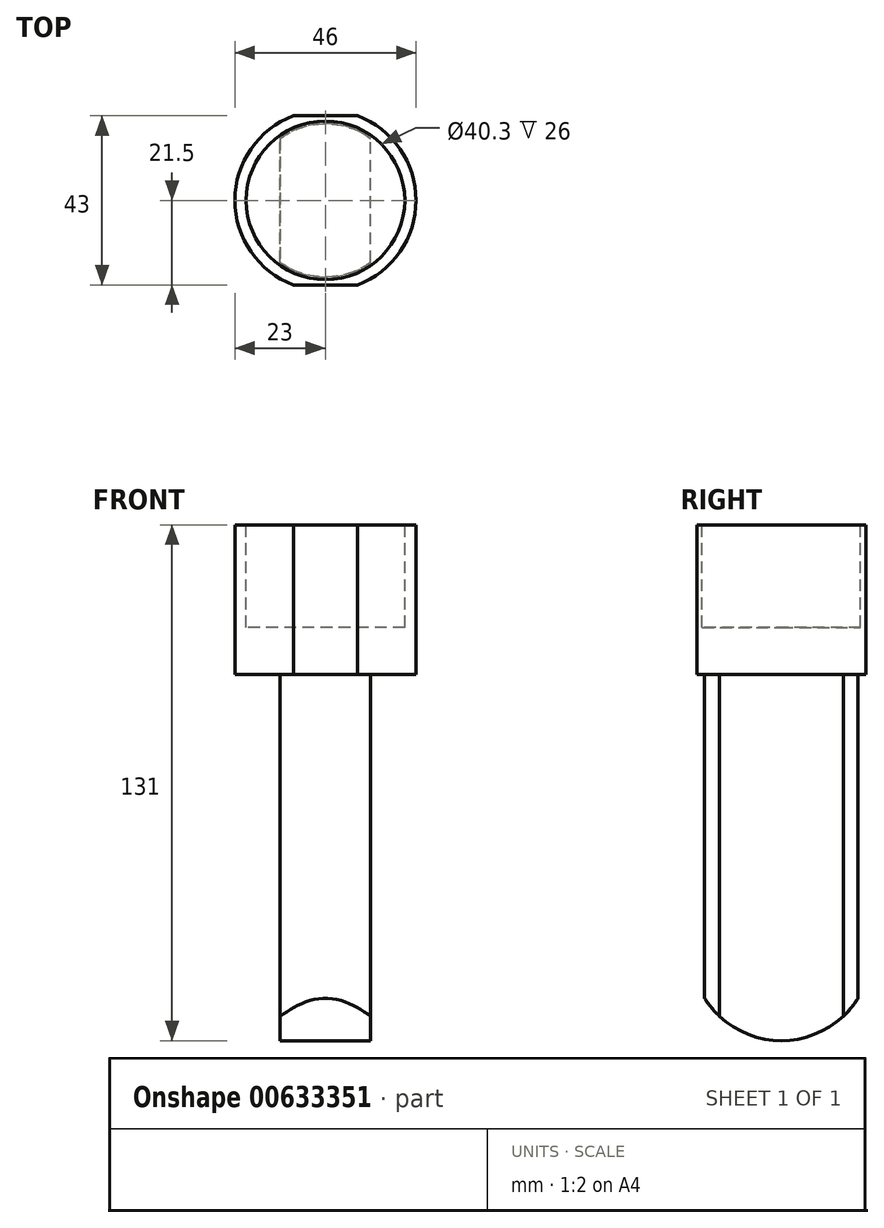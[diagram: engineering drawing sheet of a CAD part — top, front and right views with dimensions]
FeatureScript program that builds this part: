
annotation { "Feature Type Name" : "Feature", "Feature Type Description" : "" }
export const myFeature = defineFeature(function(context is Context, id is Id, definition is map)
    precondition{}
    {
        {
            var Q0;
            Q0=qCreatedBy(makeId("Top.planeOp"),FACE);
            var sketch = newSketch(context, id + "F0", { "sketchPlane" : qUnion([Q0])});
            skArc(sketch, "E0", {"start": v(8.17, -21.5) * mm, "mid": v(23, 0) * mm, "end": v(8.17, 21.5) * mm});
            skLineSegment(sketch, "E1", {"start": v(-8.17, -21.5) * mm, "end": v(8.17, -21.5) * mm});
            skLineSegment(sketch, "E2.MirrorCS", {"start": v(-8.17, 21.5) * mm, "end": v(8.17, 21.5) * mm});
            skArc(sketch, "E3.trimOffspring", {"start": v(-8.17, 21.5) * mm, "mid": v(-23, 0) * mm, "end": v(-8.17, -21.5) * mm});
            skSolve(sketch);
        }
        {
            var Q0;
            Q0 = qSketchRegion(id + "F0", true);
            extrude(context, id + "F1", {"entities" : qUnion([Q0]), "depth" : (32 + 6) * mm, "offsetDistance" : 25 * mm});
        }
        {
            var Q0;
            Q0=makeQuery(id+"F1.opExtrude","CAP_FACE",FACE,{"disambiguationData":[OSD([sQuery(id+"F0.wireOp",EDGE,"E0"),sQuery(id+"F0.wireOp",EDGE,"E1"),sQuery(id+"F0.wireOp",EDGE,"E2.MirrorCS"),sQuery(id+"F0.wireOp",EDGE,"E3.trimOffspring")])],"isStart":false});
            var sketch = newSketch(context, id + "F2", { "sketchPlane" : qUnion([Q0])});
            skCircle(sketch, "E4", {"center": v(0, 0) * mm, "radius": 20.15 * mm});
            skSolve(sketch);
        }
        {
            var Q0;
            Q0=makeQuery(id+"F2.imprint","IMPRINT",FACE,{"disambiguationData":[TD([[makeQuery(id+"F2.imprint","IMPRINT",EDGE,{"derivedFrom":sQuery(id+"F2.wireOp",EDGE,"E4")}),1.0]])]});
            extrude(context, id + "F3", {"entities" : qUnion([Q0]), "operationType" : NewBodyOperationType.REMOVE, "oppositeDirection" : true, "depth" : 26 * mm, "offsetDistance" : 25 * mm});
        }
        {
            var Q0;
            Q0=makeQuery(id+"F1.opExtrude","CAP_FACE",FACE,{"disambiguationData":[OSD([sQuery(id+"F0.wireOp",EDGE,"E0"),sQuery(id+"F0.wireOp",EDGE,"E1"),sQuery(id+"F0.wireOp",EDGE,"E2.MirrorCS"),sQuery(id+"F0.wireOp",EDGE,"E3.trimOffspring")])],"isStart":true});
            var sketch = newSketch(context, id + "F4", { "sketchPlane" : qUnion([Q0])});
            skArc(sketch, "E5", {"start": v(11.5, 15.75) * mm, "mid": v(0, 19.5) * mm, "end": v(-11.5, 15.75) * mm});
            skLineSegment(sketch, "E6", {"start": v(-11.5, 15.75) * mm, "end": v(-11.5, -15.75) * mm});
            skLineSegment(sketch, "E7.MirrorCS", {"start": v(11.5, 15.75) * mm, "end": v(11.5, -15.75) * mm});
            skArc(sketch, "E8.trimOffspring", {"start": v(-11.5, -15.75) * mm, "mid": v(0, -19.5) * mm, "end": v(11.5, -15.75) * mm});
            skSolve(sketch);
        }
        {
            var Q0;
            Q0 = qSketchRegion(id + "F4", true);
            extrude(context, id + "F5", {"entities" : qUnion([Q0]), "operationType" : NewBodyOperationType.ADD, "depth" : 93 * mm, "offsetDistance" : 25 * mm});
        }
        {
            var Q0;
            Q0=makeQuery(id+"F5.opExtrude","SWEPT_FACE",FACE,{"disambiguationData":[OSD([sQuery(id+"F4.wireOp",EDGE,"E6")])]});
            var sketch = newSketch(context, id + "F6", { "sketchPlane" : qUnion([Q0])});
            skArc(sketch, "E9", {"start": v(-22.97, -68.84) * mm, "mid": v(-1.92, -92.92) * mm, "end": v(22.84, -72.67) * mm});
            skLineSegment(sketch, "E10", {"start": v(-22.97, -68.84) * mm, "end": v(-26.97, -108.2) * mm});
            skLineSegment(sketch, "E11", {"start": v(-26.97, -108.2) * mm, "end": v(34.75, -105.52) * mm});
            skLineSegment(sketch, "E12", {"start": v(34.75, -105.52) * mm, "end": v(22.84, -72.67) * mm});
            skSolve(sketch);
        }
        {
            var Q0;
            Q0 = qSketchRegion(id + "F6", true);
            extrude(context, id + "F7", {"entities" : qUnion([Q0]), "operationType" : NewBodyOperationType.REMOVE, "endBound" : BoundingType.THROUGH_ALL, "oppositeDirection" : true, "depth" : 25 * mm, "offsetDistance" : 25 * mm});
        }
    });
